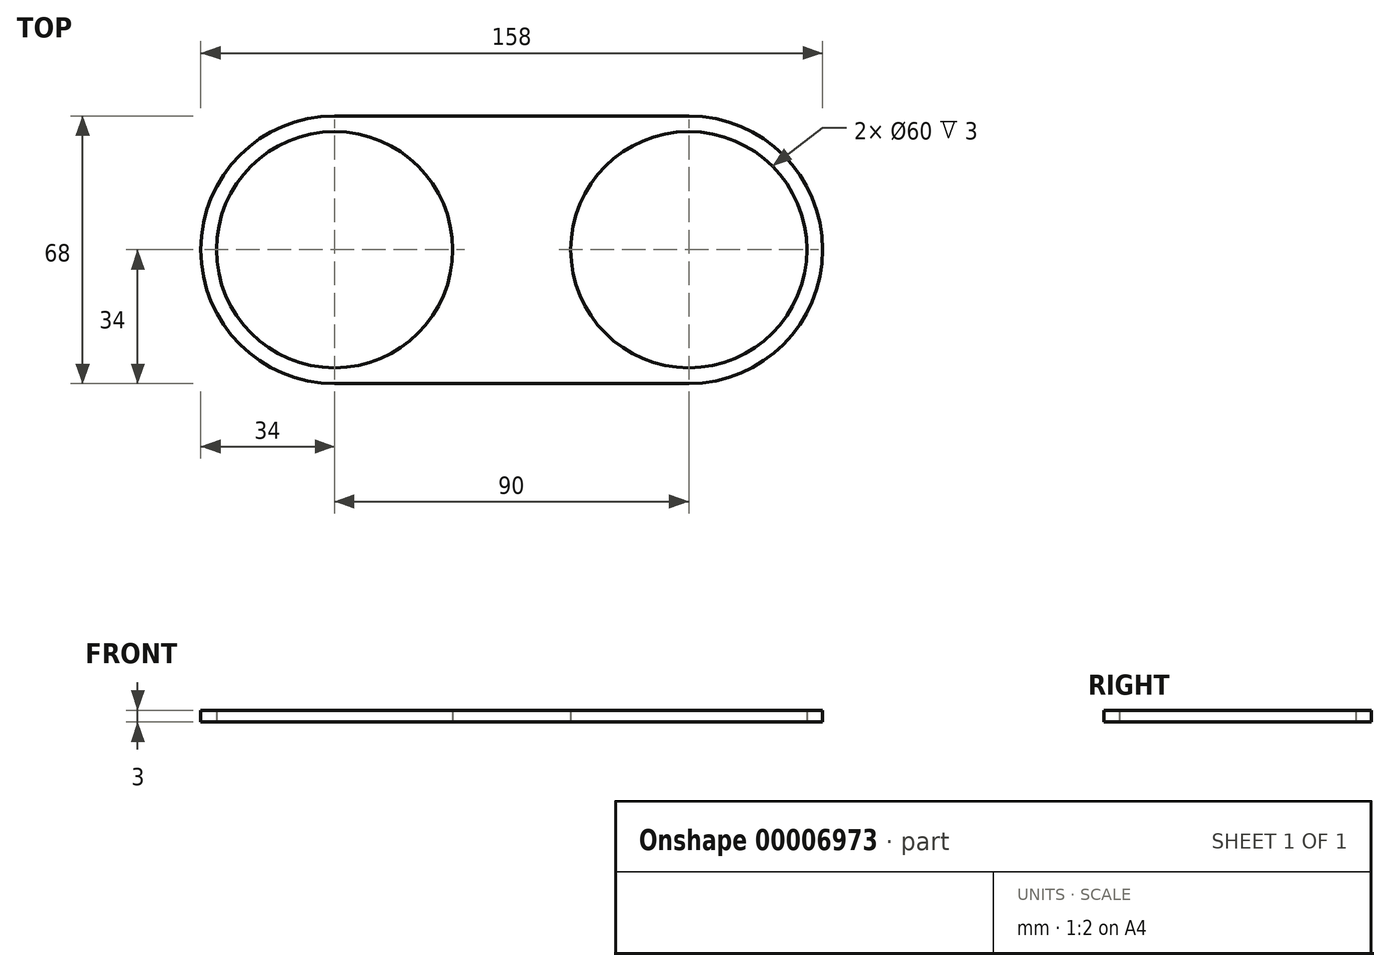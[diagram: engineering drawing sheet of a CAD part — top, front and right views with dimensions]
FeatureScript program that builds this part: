
annotation { "Feature Type Name" : "Feature", "Feature Type Description" : "" }
export const myFeature = defineFeature(function(context is Context, id is Id, definition is map)
    precondition{}
    {
        {
            var Q0;
            Q0=qCreatedBy(makeId("Top.planeOp"),FACE);
            var sketch = newSketch(context, id + "F0", { "sketchPlane" : qUnion([Q0])});
            skLineSegment(sketch, "E0.bottom", {"start": v(-45, 34) * mm, "end": v(45, 34) * mm});
            skLineSegment(sketch, "E0.top", {"start": v(-45, -34) * mm, "end": v(45, -34) * mm});
            skPoint(sketch, "E1", {"position": v(-45, 0) * mm});
            skArc(sketch, "E2", {"start": v(-45, 34) * mm, "mid": v(-79, 0) * mm, "end": v(-45, -34) * mm});
            skArc(sketch, "E3", {"start": v(45, -34) * mm, "mid": v(79, 0) * mm, "end": v(45, 34) * mm});
            skCircle(sketch, "E4", {"center": v(-45, 0) * mm, "radius": 30 * mm});
            skCircle(sketch, "E5", {"center": v(45, 0) * mm, "radius": 30 * mm});
            skSolve(sketch);
        }
        {
            var Q0;
            Q0=makeQuery(id+"F0.imprint","IMPRINT",FACE,{"disambiguationData":[TD([[makeQuery(id+"F0.imprint","IMPRINT",EDGE,{"derivedFrom":sQuery(id+"F0.wireOp",EDGE,"E0.bottom")}),-1.0]])]});
            extrude(context, id + "F1", {"entities" : qUnion([Q0]), "depth" : 3 * mm});
        }
        {
            var Q0;
            Q0=makeQuery(id+"F1.opExtrude","CAP_FACE",FACE,{"disambiguationData":[OSD([sQuery(id+"F0.wireOp",EDGE,"E0.bottom"),sQuery(id+"F0.wireOp",EDGE,"E0.top"),sQuery(id+"F0.wireOp",EDGE,"E2"),sQuery(id+"F0.wireOp",EDGE,"E3"),sQuery(id+"F0.wireOp",EDGE,"E4"),sQuery(id+"F0.wireOp",EDGE,"E5")])],"isStart":false});
            cPlane(context, id + "F2", {"entities" : qUnion([Q0]), "cplaneType" : CPlaneType.OFFSET, "offset" : 10 * mm, "width" : 150 * mm, "height" : 150 * mm});
        }
    });
